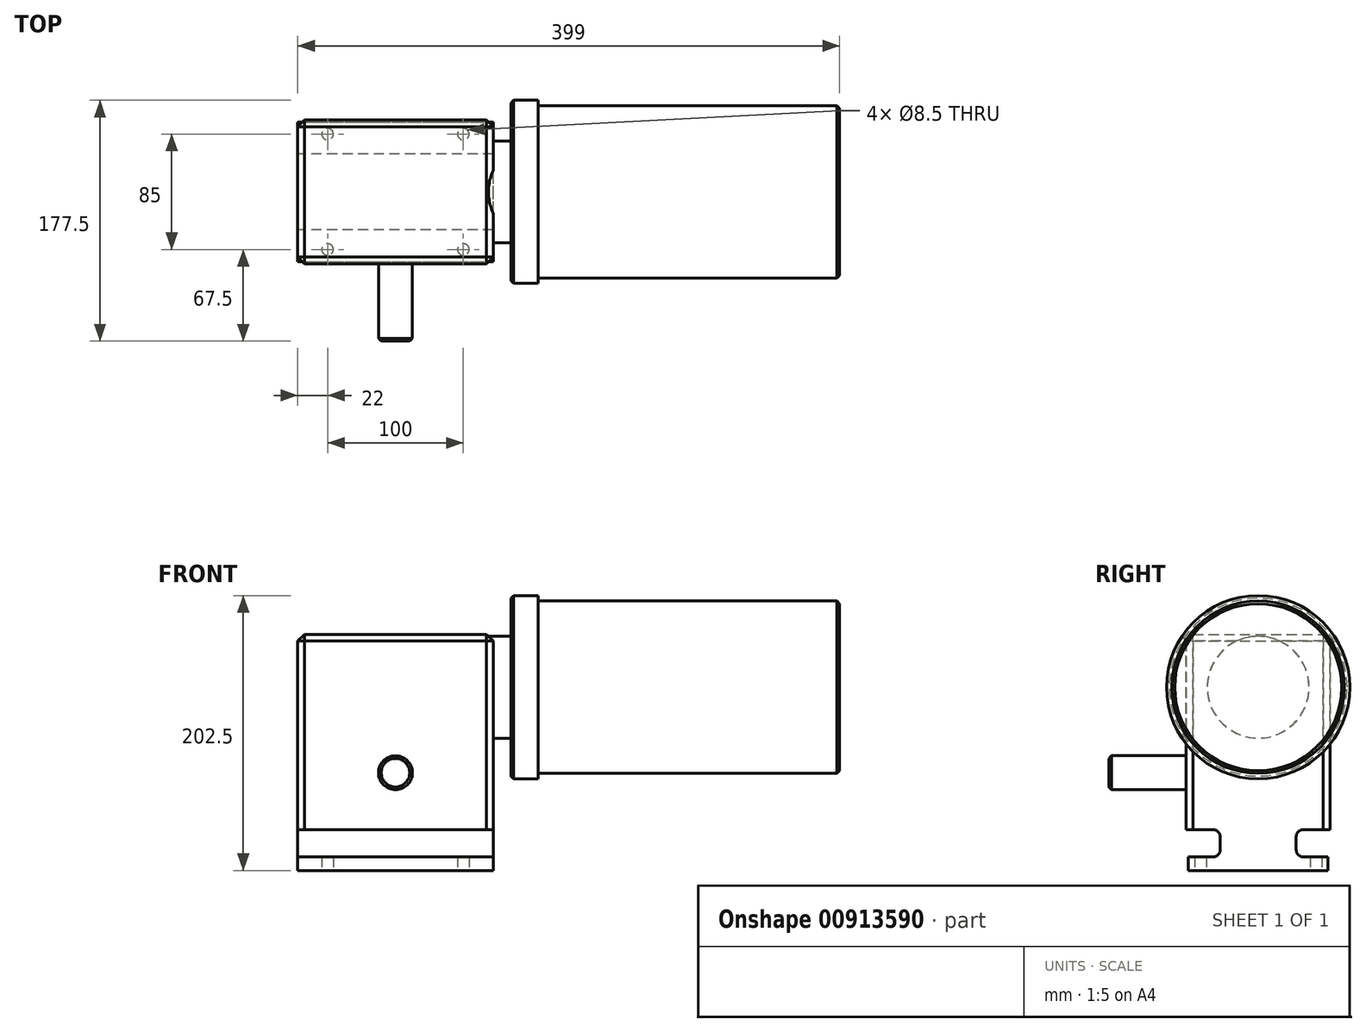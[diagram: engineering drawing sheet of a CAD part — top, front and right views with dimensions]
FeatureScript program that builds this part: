
annotation { "Feature Type Name" : "Feature", "Feature Type Description" : "" }
export const myFeature = defineFeature(function(context is Context, id is Id, definition is map)
    precondition{}
    {
        {
            var Q0;
            Q0=qCreatedBy(makeId("Front.planeOp"),FACE);
            var sketch = newSketch(context, id + "F0", { "sketchPlane" : qUnion([Q0])});
            skLineSegment(sketch, "E0.rect.bottom", {"start": v(72, 87) * mm, "end": v(-72, 87) * mm});
            skLineSegment(sketch, "E0.rect.top", {"start": v(72, -87) * mm, "end": v(-72, -87) * mm});
            skLineSegment(sketch, "E0.rect.left", {"start": v(72, 87) * mm, "end": v(72, -87) * mm});
            skLineSegment(sketch, "E0.rect.right", {"start": v(-72, 87) * mm, "end": v(-72, -87) * mm});
            skPoint(sketch, "E0.rect.middle", {"position": v(0, 0) * mm});
            skSolve(sketch);
        }
        {
            var Q0;
            Q0=qSketchRegion(id+"F0",true);
            extrude(context, id + "F1", {"entities" : qUnion([Q0]), "depth" : 106 * mm});
        }
        {
            var Q0;
            Q0=makeQuery(id+"F1.opExtrude","CAP_FACE",FACE,{"disambiguationData":[OSD([sQuery(id+"F0.wireOp",EDGE,"E0.rect.bottom"),sQuery(id+"F0.wireOp",EDGE,"E0.rect.top"),sQuery(id+"F0.wireOp",EDGE,"E0.rect.left"),sQuery(id+"F0.wireOp",EDGE,"E0.rect.right")])],"isStart":false});
            var sketch = newSketch(context, id + "F2", { "sketchPlane" : qUnion([Q0])});
            skCircle(sketch, "E1", {"center": v(0, -15) * mm, "radius": 40 * mm, "construction": true});
            skLineSegment(sketch, "E2", {"start": v(0, 0) * mm, "end": v(0, -15) * mm, "construction": true});
            skCircle(sketch, "E3", {"center": v(0, -15) * mm, "radius": 12.5 * mm});
            skSolve(sketch);
        }
        {
            var Q0;
            Q0=makeQuery(id+"F1.opExtrude","SWEPT_FACE",FACE,{"disambiguationData":[OSD([sQuery(id+"F0.wireOp",EDGE,"E0.rect.top")])]});
            var sketch = newSketch(context, id + "F3", { "sketchPlane" : qUnion([Q0])});
            skLineSegment(sketch, "E4", {"start": v(-72, 0) * mm, "end": v(72, 106) * mm, "construction": true});
            skLineSegment(sketch, "E5.rect.bottom", {"start": v(-72, 104.5) * mm, "end": v(72, 104.5) * mm});
            skLineSegment(sketch, "E5.rect.top", {"start": v(-72, 1.5) * mm, "end": v(72, 1.5) * mm});
            skLineSegment(sketch, "E5.rect.left", {"start": v(-72, 104.5) * mm, "end": v(-72, 1.5) * mm});
            skLineSegment(sketch, "E5.rect.right", {"start": v(72, 104.5) * mm, "end": v(72, 1.5) * mm});
            skPoint(sketch, "E5.rect.middle", {"position": v(0, 53) * mm});
            skSolve(sketch);
        }
        {
            var Q0;
            {var subQ0=sQuery(id+"F3.wireOp",EDGE,"E5.rect.bottom");Q0=makeQuery(id+"F3.imprint","IMPRINT",FACE,{"disambiguationData":[TD([[makeQuery(id+"F3.imprint","IMPRINT",EDGE,{"derivedFrom":subQ0}),1.0]])]});}
            var Q1;
            {var subQ0=sQuery(id+"F3.wireOp",EDGE,"E5.rect.top");Q1=makeQuery(id+"F3.imprint","IMPRINT",FACE,{"disambiguationData":[TD([[makeQuery(id+"F3.imprint","IMPRINT",EDGE,{"derivedFrom":subQ0}),-1.0]])]});}
            extrude(context, id + "F4", {"entities" : qUnion([Q0, Q1]), "operationType" : NewBodyOperationType.REMOVE, "oppositeDirection" : true, "depth" : 10 * mm});
        }
        {
            var Q0;
            Q0=makeQuery(id+"F1.opExtrude","SWEPT_FACE",FACE,{"disambiguationData":[OSD([sQuery(id+"F0.wireOp",EDGE,"E0.rect.top")])]});
            var sketch = newSketch(context, id + "F5", { "sketchPlane" : qUnion([Q0])});
            skLineSegment(sketch, "E6", {"start": v(-72, 104.5) * mm, "end": v(72, 1.5) * mm, "construction": true});
            skLineSegment(sketch, "E7.rect.bottom", {"start": v(50, 95.5) * mm, "end": v(-50, 95.5) * mm, "construction": true});
            skLineSegment(sketch, "E7.rect.top", {"start": v(50, 10.5) * mm, "end": v(-50, 10.5) * mm, "construction": true});
            skLineSegment(sketch, "E7.rect.left", {"start": v(50, 95.5) * mm, "end": v(50, 10.5) * mm, "construction": true});
            skLineSegment(sketch, "E7.rect.right", {"start": v(-50, 95.5) * mm, "end": v(-50, 10.5) * mm, "construction": true});
            skPoint(sketch, "E7.rect.middle", {"position": v(0, 53) * mm});
            skCircle(sketch, "E8", {"center": v(-50, 95.5) * mm, "radius": 4.25 * mm});
            skCircle(sketch, "E9", {"center": v(50, 95.5) * mm, "radius": 4.25 * mm});
            skCircle(sketch, "E10", {"center": v(50, 10.5) * mm, "radius": 4.25 * mm});
            skCircle(sketch, "E11", {"center": v(-50, 10.5) * mm, "radius": 4.25 * mm});
            skSolve(sketch);
        }
        {
            var Q0;
            Q0=qSketchRegion(id+"F5",true);
            extrude(context, id + "F6", {"entities" : qUnion([Q0]), "operationType" : NewBodyOperationType.REMOVE, "oppositeDirection" : true, "depth" : 10 * mm});
        }
        {
            var Q0;
            Q0=makeQuery(id+"F1.opExtrude","SWEPT_FACE",FACE,{"disambiguationData":[OSD([sQuery(id+"F0.wireOp",EDGE,"E0.rect.right")])]});
            var sketch = newSketch(context, id + "F7", { "sketchPlane" : qUnion([Q0])});
            skLineSegment(sketch, "E12.bottom", {"start": v(0, -77) * mm, "end": v(25, -77) * mm});
            skLineSegment(sketch, "E12.top", {"start": v(0, -57) * mm, "end": v(25, -57) * mm});
            skLineSegment(sketch, "E12.left", {"start": v(0, -77) * mm, "end": v(0, -57) * mm});
            skLineSegment(sketch, "E12.right", {"start": v(25, -77) * mm, "end": v(25, -57) * mm});
            skLineSegment(sketch, "E13", {"start": v(53, -87) * mm, "end": v(53, 87) * mm, "construction": true});
            skLineSegment(sketch, "E14.MirrorCS", {"start": v(81, -77) * mm, "end": v(81, -57) * mm});
            skLineSegment(sketch, "E15.MirrorCS", {"start": v(106, -57) * mm, "end": v(81, -57) * mm});
            skLineSegment(sketch, "E16.MirrorCS", {"start": v(106, -77) * mm, "end": v(106, -57) * mm});
            skLineSegment(sketch, "E17.MirrorCS", {"start": v(106, -77) * mm, "end": v(81, -77) * mm});
            skSolve(sketch);
        }
        {
            var Q0;
            Q0=qSketchRegion(id+"F7",true);
            extrude(context, id + "F8", {"entities" : qUnion([Q0]), "operationType" : NewBodyOperationType.REMOVE, "endBound" : BoundingType.THROUGH_ALL, "oppositeDirection" : true, "depth" : 25 * mm});
        }
        {
            var Q0;
            Q0=qCreatedBy(makeId("Right.planeOp"),FACE);
            cPlane(context, id + "F9", {"entities" : qUnion([Q0]), "cplaneType" : CPlaneType.OFFSET, "offset" : 95 * mm, "width" : 150 * mm, "height" : 150 * mm});
        }
        {
            var Q0;
            Q0=qCreatedBy(id+"F9.planeOp",FACE);
            var sketch = newSketch(context, id + "F10", { "sketchPlane" : qUnion([Q0])});
            skLineSegment(sketch, "E18.0", {"start": v(-104.5, -87) * mm, "end": v(-1.5, -87) * mm, "construction": true});
            skLineSegment(sketch, "E19", {"start": v(-53, -87) * mm, "end": v(-53, 83.36) * mm, "construction": true});
            skCircle(sketch, "E20", {"center": v(-53, 48) * mm, "radius": 67.5 * mm});
            skSolve(sketch);
        }
        {
            var Q0;
            Q0=qSketchRegion(id+"F10",true);
            extrude(context, id + "F11", {"entities" : qUnion([Q0]), "operationType" : NewBodyOperationType.ADD, "oppositeDirection" : true, "depth" : 10 * mm});
        }
        {
            var Q0;
            Q0=makeQuery(id+"F11.opExtrude","CAP_FACE",FACE,{"disambiguationData":[OSD([sQuery(id+"F10.wireOp",EDGE,"E20")])],"isStart":false});
            var sketch = newSketch(context, id + "F12", { "sketchPlane" : qUnion([Q0])});
            skCircle(sketch, "E21", {"center": v(53, 48) * mm, "radius": 37.5 * mm});
            skSolve(sketch);
        }
        {
            var Q0;
            Q0=qSketchRegion(id+"F12",true);
            extrude(context, id + "F13", {"entities" : qUnion([Q0]), "operationType" : NewBodyOperationType.ADD, "endBound" : BoundingType.UP_TO_NEXT, "depth" : 25 * mm});
        }
        {
            var Q0;
            Q0=makeQuery(id+"F11.opExtrude","CAP_FACE",FACE,{"disambiguationData":[OSD([sQuery(id+"F10.wireOp",EDGE,"E20")])],"isStart":true});
            var sketch = newSketch(context, id + "F14", { "sketchPlane" : qUnion([Q0])});
            skCircle(sketch, "E22.0", {"center": v(-53, 48) * mm, "radius": 67.5 * mm});
            skSolve(sketch);
        }
        {
            var Q0;
            Q0=qSketchRegion(id+"F14",true);
            extrude(context, id + "F15", {"entities" : qUnion([Q0]), "operationType" : NewBodyOperationType.ADD, "depth" : 10 * mm});
        }
        {
            var Q0;
            Q0=makeQuery(id+"F15.opExtrude","CAP_FACE",FACE,{"disambiguationData":[OSD([sQuery(id+"F14.wireOp",EDGE,"E22.0")])],"isStart":false});
            var sketch = newSketch(context, id + "F16", { "sketchPlane" : qUnion([Q0])});
            skCircle(sketch, "E23", {"center": v(-53, 48) * mm, "radius": 63.5 * mm});
            skSolve(sketch);
        }
        {
            var Q0;
            Q0=qSketchRegion(id+"F16",true);
            extrude(context, id + "F17", {"entities" : qUnion([Q0]), "operationType" : NewBodyOperationType.ADD, "depth" : 222 * mm});
        }
        {
            var Q0;
            Q0=qSketchRegion(id+"F2",true);
            extrude(context, id + "F18", {"entities" : qUnion([Q0]), "operationType" : NewBodyOperationType.ADD, "depth" : 57 * mm});
        }
        {
            var Q0;
            Q0=makeQuery(id+"F18.opExtrude","CAP_EDGE",EDGE,{"disambiguationData":[OSD([sQuery(id+"F2.wireOp",EDGE,"E3")])],"isStart":false});
            var Q1;
            Q1=makeQuery(id+"F17.opExtrude","CAP_EDGE",EDGE,{"disambiguationData":[OSD([sQuery(id+"F16.wireOp",EDGE,"E23")])],"isStart":false});
            var Q2;
            Q2=makeQuery(id+"F11.opExtrude","CAP_EDGE",EDGE,{"disambiguationData":[OSD([sQuery(id+"F10.wireOp",EDGE,"E20")])],"isStart":false});
            chamfer(context, id + "F19", {"entities" : qUnion([Q0, Q1, Q2]), "width" : 2 * mm, "tangentPropagation" : true});
        }
        {
            var Q0;
            Q0=makeQuery(id+"F1.opExtrude","SWEPT_EDGE",EDGE,{"disambiguationData":[OSD([sQuery(id+"F0.wireOp",EDGE,"E0.rect.bottom"),sQuery(id+"F0.wireOp",EDGE,"E0.rect.right")])]});
            var Q1;
            Q1=makeQuery(id+"F1.opExtrude","SWEPT_EDGE",EDGE,{"disambiguationData":[OSD([sQuery(id+"F0.wireOp",EDGE,"E0.rect.bottom"),sQuery(id+"F0.wireOp",EDGE,"E0.rect.left")])]});
            var Q2;
            Q2=makeQuery(id+"F1.opExtrude","CAP_EDGE",EDGE,{"disambiguationData":[OSD([sQuery(id+"F0.wireOp",EDGE,"E0.rect.right")])],"isStart":false});
            var Q3;
            Q3=makeQuery(id+"F1.opExtrude","CAP_EDGE",EDGE,{"disambiguationData":[OSD([sQuery(id+"F0.wireOp",EDGE,"E0.rect.right")])],"isStart":true});
            var Q4;
            Q4=makeQuery(id+"F1.opExtrude","CAP_EDGE",EDGE,{"disambiguationData":[OSD([sQuery(id+"F0.wireOp",EDGE,"E0.rect.left")])],"isStart":false});
            var Q5;
            Q5=makeQuery(id+"F1.opExtrude","CAP_EDGE",EDGE,{"disambiguationData":[OSD([sQuery(id+"F0.wireOp",EDGE,"E0.rect.left")])],"isStart":true});
            var Q6;
            Q6=makeQuery(id+"F1.opExtrude","CAP_EDGE",EDGE,{"disambiguationData":[OSD([sQuery(id+"F0.wireOp",EDGE,"E0.rect.bottom")])],"isStart":false});
            var Q7;
            Q7=makeQuery(id+"F1.opExtrude","CAP_EDGE",EDGE,{"disambiguationData":[OSD([sQuery(id+"F0.wireOp",EDGE,"E0.rect.bottom")])],"isStart":true});
            chamfer(context, id + "F20", {"entities" : qUnion([Q0, Q1, Q2, Q3, Q4, Q5, Q6, Q7]), "width" : 5 * mm, "tangentPropagation" : true});
        }
        {
            var Q0;
            Q0=makeQuery(id+"F8.boolean.opBoolean","COPY",EDGE,{"derivedFrom":makeQuery(id+"F8.opExtrude","SWEPT_EDGE",EDGE,{"disambiguationData":[OSD([sQuery(id+"F7.wireOp",EDGE,"E14.MirrorCS"),sQuery(id+"F7.wireOp",EDGE,"E15.MirrorCS")])]})});
            var Q1;
            Q1=makeQuery(id+"F8.boolean.opBoolean","COPY",EDGE,{"derivedFrom":makeQuery(id+"F8.opExtrude","SWEPT_EDGE",EDGE,{"disambiguationData":[OSD([sQuery(id+"F7.wireOp",EDGE,"E14.MirrorCS"),sQuery(id+"F7.wireOp",EDGE,"E17.MirrorCS")])]})});
            var Q2;
            Q2=makeQuery(id+"F8.boolean.opBoolean","COPY",EDGE,{"derivedFrom":makeQuery(id+"F8.opExtrude","SWEPT_EDGE",EDGE,{"disambiguationData":[OSD([sQuery(id+"F7.wireOp",EDGE,"E12.top"),sQuery(id+"F7.wireOp",EDGE,"E12.right")])]})});
            var Q3;
            Q3=makeQuery(id+"F8.boolean.opBoolean","COPY",EDGE,{"derivedFrom":makeQuery(id+"F8.opExtrude","SWEPT_EDGE",EDGE,{"disambiguationData":[OSD([sQuery(id+"F7.wireOp",EDGE,"E12.bottom"),sQuery(id+"F7.wireOp",EDGE,"E12.right")])]})});
            fillet(context, id + "F21", {"entities" : qUnion([Q0, Q1, Q2, Q3]), "radius" : 5 * mm, "tangentPropagation" : true, "allowEdgeOverflow" : false});
        }
    });
